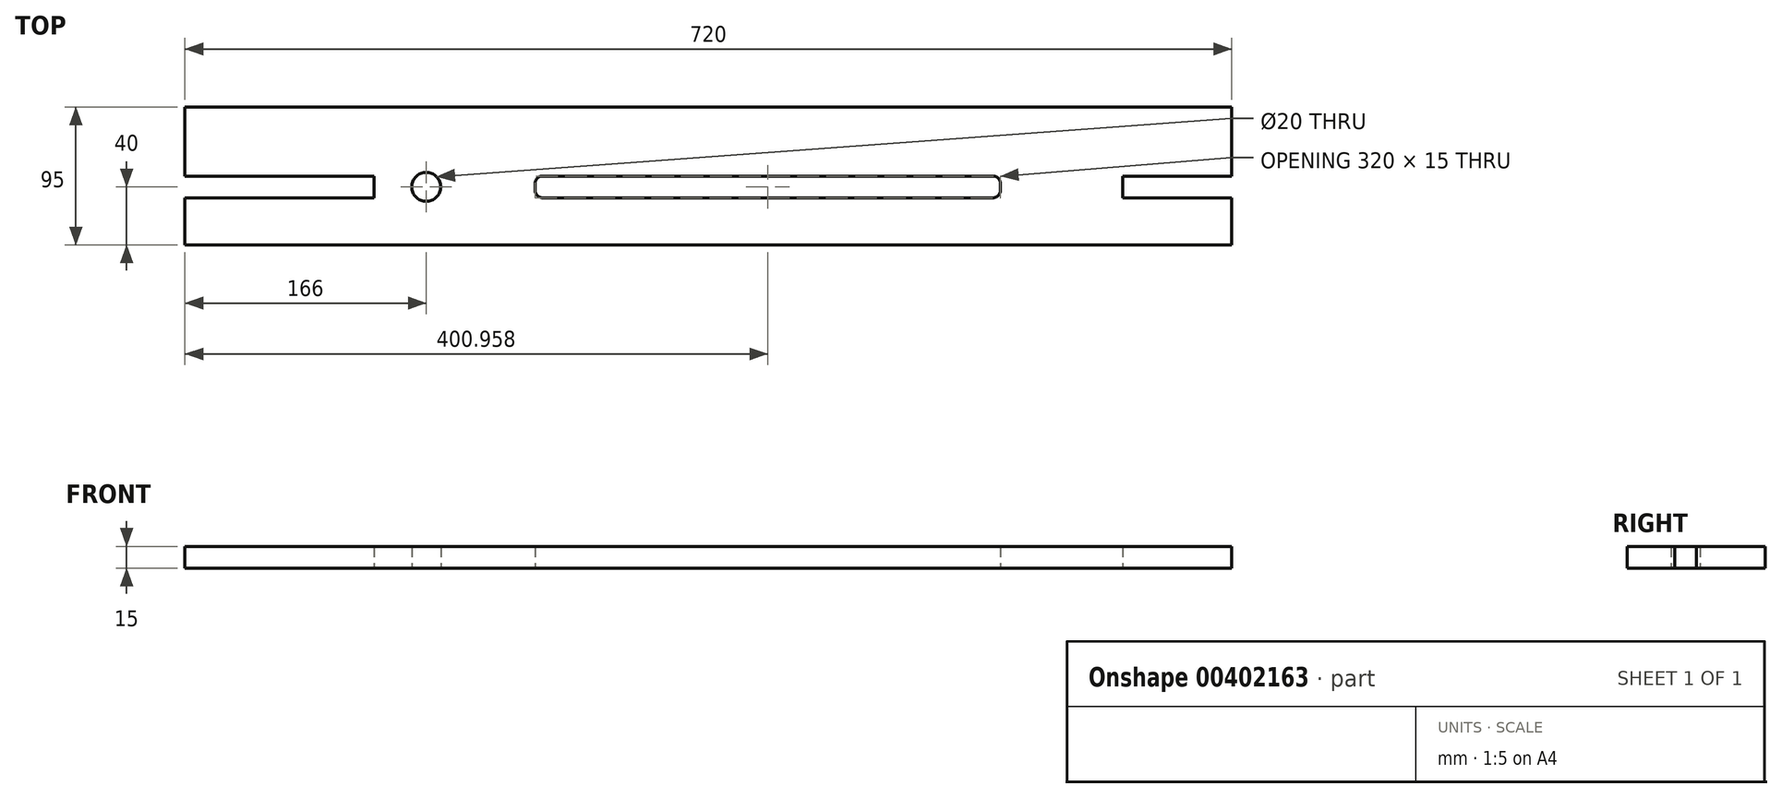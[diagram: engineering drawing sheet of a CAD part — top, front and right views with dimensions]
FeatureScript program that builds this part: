
annotation { "Feature Type Name" : "Feature", "Feature Type Description" : "" }
export const myFeature = defineFeature(function(context is Context, id is Id, definition is map)
    precondition{}
    {
        {
            var Q0;
            Q0=qCreatedBy(makeId("Top.planeOp"),FACE);
            var sketch = newSketch(context, id + "F0", { "sketchPlane" : qUnion([Q0])});
            skLineSegment(sketch, "E0.bottom", {"start": v(-360, 0) * mm, "end": v(360, 0) * mm});
            skLineSegment(sketch, "E0.top", {"start": v(-360, 95) * mm, "end": v(360, 95) * mm});
            skLineSegment(sketch, "E0.left", {"start": v(-360, 0) * mm, "end": v(-360, 32.5) * mm});
            skLineSegment(sketch, "E0.right", {"start": v(360, 0) * mm, "end": v(360, 32.5) * mm});
            skLineSegment(sketch, "E1", {"start": v(-360, 32.5) * mm, "end": v(-230, 32.5) * mm});
            skLineSegment(sketch, "E2", {"start": v(-230, 32.5) * mm, "end": v(-230, 47.5) * mm});
            skLineSegment(sketch, "E3", {"start": v(-230, 47.5) * mm, "end": v(-360, 47.5) * mm});
            skLineSegment(sketch, "E4", {"start": v(360, 32.5) * mm, "end": v(285, 32.5) * mm});
            skLineSegment(sketch, "E5", {"start": v(285, 32.5) * mm, "end": v(285, 47.5) * mm});
            skLineSegment(sketch, "E6", {"start": v(285, 47.5) * mm, "end": v(360, 47.5) * mm});
            skLineSegment(sketch, "E7.trimOffspring", {"start": v(-360, 47.5) * mm, "end": v(-360, 95) * mm});
            skLineSegment(sketch, "E8.trimOffspring", {"start": v(360, 47.5) * mm, "end": v(360, 95) * mm});
            skCircle(sketch, "E9", {"center": v(-194, 40) * mm, "radius": 10 * mm});
            skPoint(sketch, "E9.centerSnap0", {"position": v(-230, 40) * mm});
            skLineSegment(sketch, "E10.bottom", {"start": v(-114.04, 47.5) * mm, "end": v(195.96, 47.5) * mm});
            skLineSegment(sketch, "E10.top", {"start": v(-114.04, 32.5) * mm, "end": v(195.96, 32.5) * mm});
            skLineSegment(sketch, "E10.left", {"start": v(-119.04, 42.5) * mm, "end": v(-119.04, 37.5) * mm});
            skLineSegment(sketch, "E10.right", {"start": v(200.96, 42.5) * mm, "end": v(200.96, 37.5) * mm});
            skPoint(sketch, "E11.visualSharp", {"position": v(-119.04, 47.5) * mm});
            skArc(sketch, "E11.filletArc", {"start": v(-114.04, 47.5) * mm, "mid": v(-117.58, 46.04) * mm, "end": v(-119.04, 42.5) * mm});
            skPoint(sketch, "E12.visualSharp", {"position": v(-119.04, 32.5) * mm});
            skArc(sketch, "E12.filletArc", {"start": v(-119.04, 37.5) * mm, "mid": v(-117.58, 33.96) * mm, "end": v(-114.04, 32.5) * mm});
            skPoint(sketch, "E13.visualSharp", {"position": v(200.96, 32.5) * mm});
            skArc(sketch, "E13.filletArc", {"start": v(195.96, 32.5) * mm, "mid": v(199.5, 33.96) * mm, "end": v(200.96, 37.5) * mm});
            skPoint(sketch, "E14.visualSharp", {"position": v(200.96, 47.5) * mm});
            skArc(sketch, "E14.filletArc", {"start": v(200.96, 42.5) * mm, "mid": v(199.5, 46.04) * mm, "end": v(195.96, 47.5) * mm});
            skSolve(sketch);
        }
        {
            var Q0;
            Q0 = qSketchRegion(id + "F0", true);
            extrude(context, id + "F1", {"entities" : qUnion([Q0]), "depth" : 15 * mm});
        }
    });
